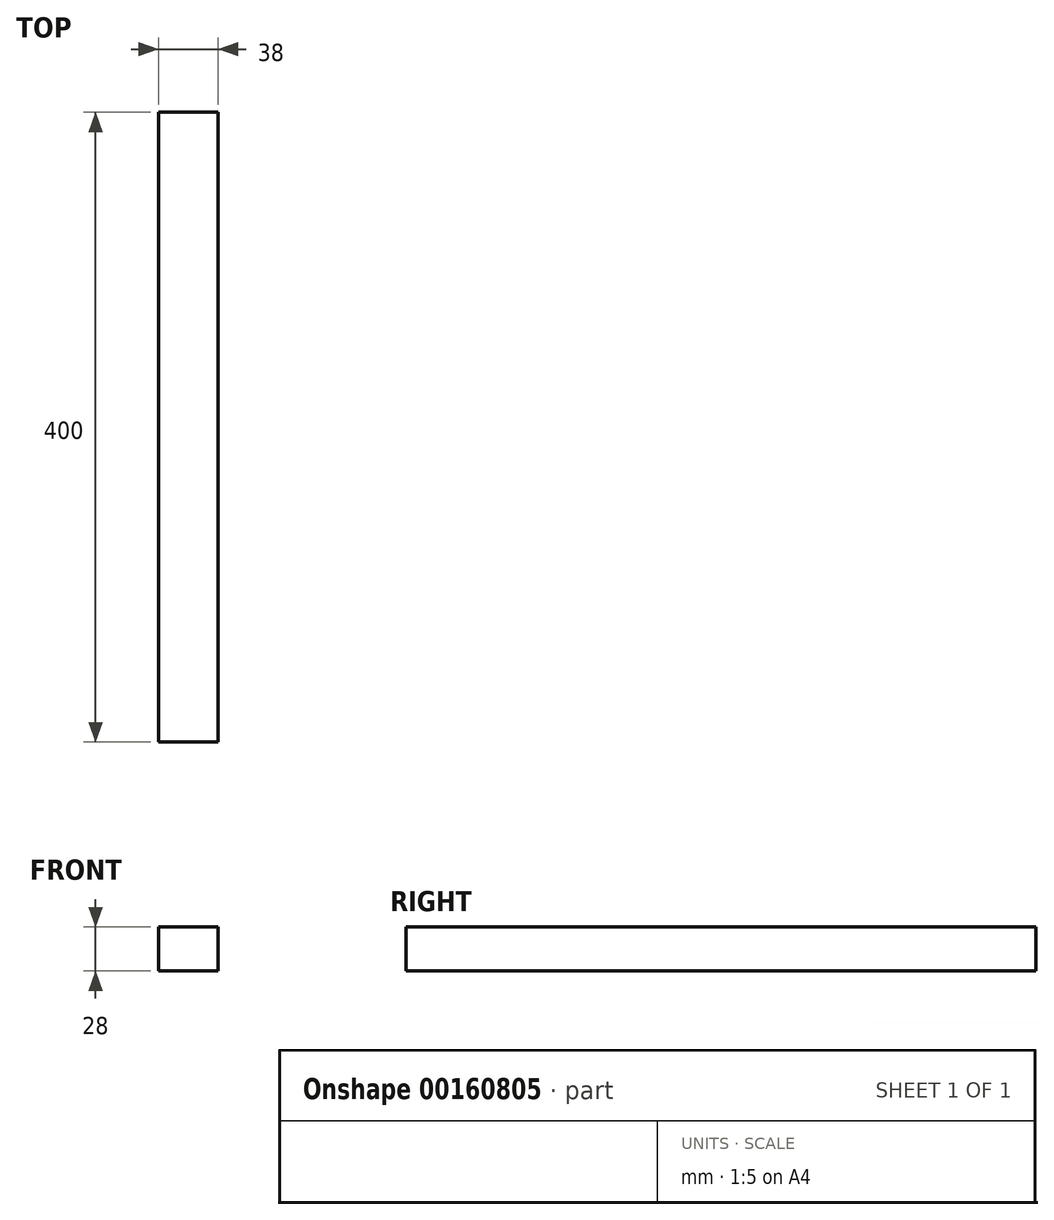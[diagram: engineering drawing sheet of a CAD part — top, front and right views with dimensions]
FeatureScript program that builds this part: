
annotation { "Feature Type Name" : "Feature", "Feature Type Description" : "" }
export const myFeature = defineFeature(function(context is Context, id is Id, definition is map)
    precondition{}
    {
        {
            var Q0;
            Q0=qCreatedBy(makeId("Front.planeOp"),FACE);
            var sketch = newSketch(context, id + "F0", { "sketchPlane" : qUnion([Q0])});
            skLineSegment(sketch, "E0.bottom", {"start": v(-107.59, -0.66) * mm, "end": v(-69.59, -0.66) * mm});
            skLineSegment(sketch, "E0.top", {"start": v(-107.59, -28.66) * mm, "end": v(-69.59, -28.66) * mm});
            skLineSegment(sketch, "E0.left", {"start": v(-107.59, -0.66) * mm, "end": v(-107.59, -28.66) * mm});
            skLineSegment(sketch, "E0.right", {"start": v(-69.59, -0.66) * mm, "end": v(-69.59, -28.66) * mm});
            skSolve(sketch);
        }
        {
            var Q0;
            Q0=makeQuery(id+"F0.imprint","IMPRINT",FACE,{"disambiguationData":[TD([[makeQuery(id+"F0.imprint","IMPRINT",EDGE,{"derivedFrom":sQuery(id+"F0.wireOp",EDGE,"E0.bottom")}),-1.0]])]});
            extrude(context, id + "F1", {"entities" : qUnion([Q0]), "depth" : 400 * mm});
        }
    });
